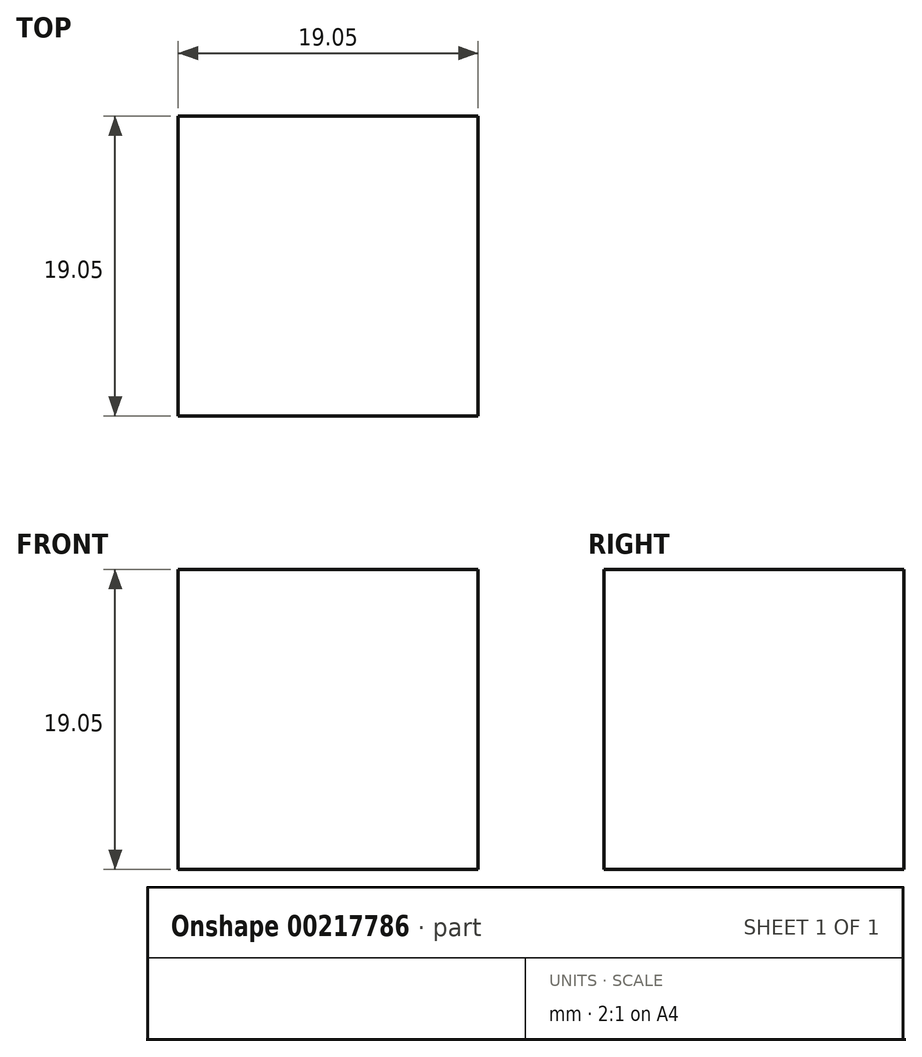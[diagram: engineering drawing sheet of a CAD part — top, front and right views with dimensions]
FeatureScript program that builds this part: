
annotation { "Feature Type Name" : "Feature", "Feature Type Description" : "" }
export const myFeature = defineFeature(function(context is Context, id is Id, definition is map)
    precondition{}
    {
        {
            var Q0;
            Q0=qCreatedBy(makeId("Front.planeOp"),FACE);
            var sketch = newSketch(context, id + "F0", { "sketchPlane" : qUnion([Q0])});
            skLineSegment(sketch, "E0.bottom", {"start": v(0, 0) * mm, "end": v(19.05, 0) * mm});
            skLineSegment(sketch, "E0.top", {"start": v(0, 19.05) * mm, "end": v(19.05, 19.05) * mm});
            skLineSegment(sketch, "E0.left", {"start": v(0, 0) * mm, "end": v(0, 19.05) * mm});
            skLineSegment(sketch, "E0.right", {"start": v(19.05, 0) * mm, "end": v(19.05, 19.05) * mm});
            skSolve(sketch);
        }
        {
            var Q0;
            Q0=makeQuery(id+"F0.imprint","IMPRINT",FACE,{"disambiguationData":[TD([[makeQuery(id+"F0.imprint","IMPRINT",EDGE,{"derivedFrom":sQuery(id+"F0.wireOp",EDGE,"E0.bottom")}),1.0]])]});
            extrude(context, id + "F1", {"entities" : qUnion([Q0]), "depth" : 19.05 * mm});
        }
    });
